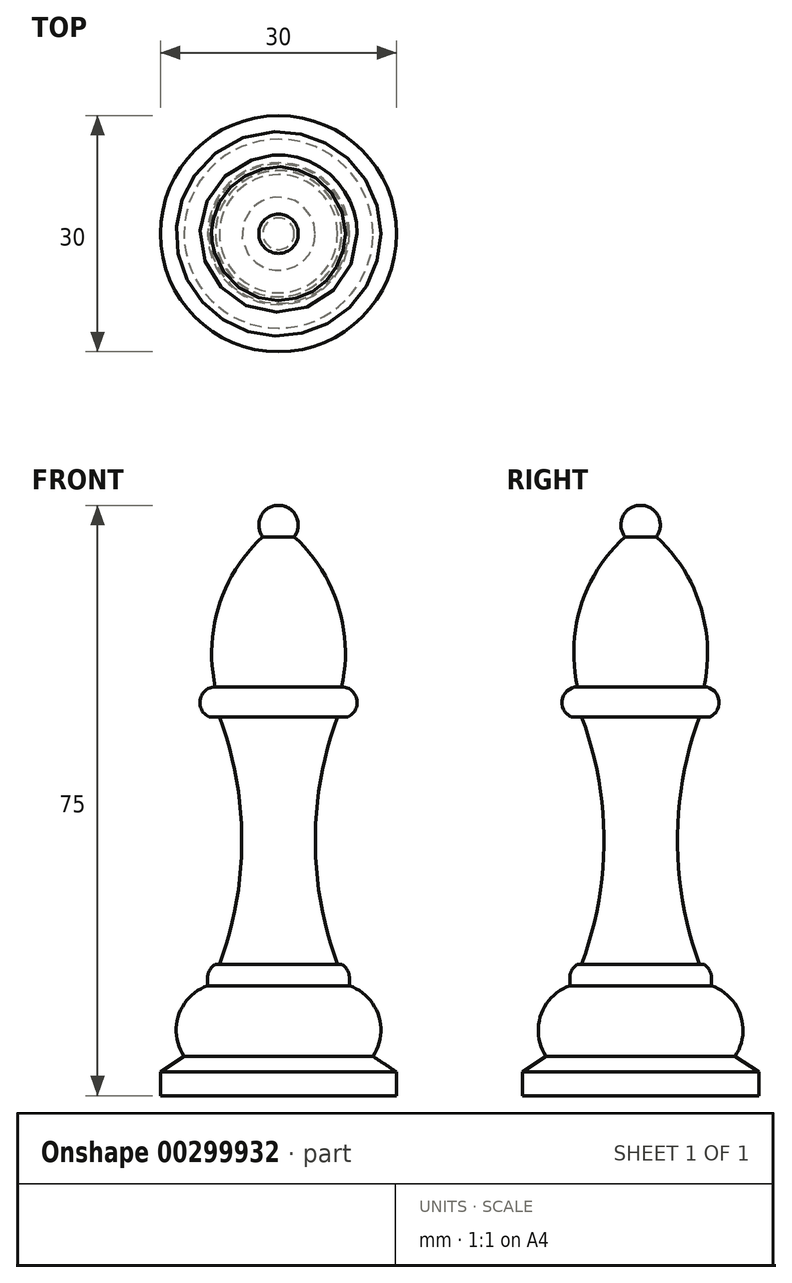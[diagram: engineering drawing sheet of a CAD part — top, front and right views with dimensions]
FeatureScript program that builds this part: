
annotation { "Feature Type Name" : "Feature", "Feature Type Description" : "" }
export const myFeature = defineFeature(function(context is Context, id is Id, definition is map)
    precondition{}
    {
        {
            var Q0;
            Q0=qCreatedBy(makeId("Front.planeOp"),FACE);
            var sketch = newSketch(context, id + "F0", { "sketchPlane" : qUnion([Q0])});
            skLineSegment(sketch, "E0", {"start": v(0, 0) * mm, "end": v(0, -75) * mm});
            skArc(sketch, "E1", {"start": v(2, -4) * mm, "mid": v(2.24, -1.38) * mm, "end": v(0, 0) * mm});
            skArc(sketch, "E2", {"start": v(8.03, -23.06) * mm, "mid": v(7.57, -12.72) * mm, "end": v(2, -4) * mm});
            skArc(sketch, "E3", {"start": v(12, -70) * mm, "mid": v(12.69, -64.78) * mm, "end": v(9, -61.03) * mm});
            skLineSegment(sketch, "E4", {"start": v(12, -70) * mm, "end": v(15, -72) * mm});
            skLineSegment(sketch, "E5", {"start": v(15, -72) * mm, "end": v(15, -75) * mm});
            skLineSegment(sketch, "E6", {"start": v(15, -75) * mm, "end": v(0, -75) * mm});
            skLineSegment(sketch, "E7", {"start": v(9, -61.03) * mm, "end": v(9, -60.03) * mm});
            skArc(sketch, "E8", {"start": v(9, -60.03) * mm, "mid": v(8.73, -59.03) * mm, "end": v(8, -58.3) * mm});
            skArc(sketch, "E9", {"start": v(8.84, -26.87) * mm, "mid": v(9.94, -24.65) * mm, "end": v(8.03, -23.06) * mm});
            skLineSegment(sketch, "E10", {"start": v(8.84, -26.87) * mm, "end": v(7.5, -26.87) * mm});
            skArc(sketch, "E11", {"start": v(7.5, -26.87) * mm, "mid": v(4.67, -42.58) * mm, "end": v(7.5, -58.3) * mm});
            skLineSegment(sketch, "E12", {"start": v(7.5, -58.3) * mm, "end": v(8, -58.3) * mm});
            skSolve(sketch);
        }
        {
            var Q0;
            Q0 = qSketchRegion(id + "F0", true);
            var Q1;
            Q1=sQuery(id+"F0.wireOp",EDGE,"E0");
            revolve(context, id + "F1", {"entities" : qUnion([Q0]), "axis" : qUnion([Q1]), "revolveType" : RevolveType.FULL});
        }
    });
